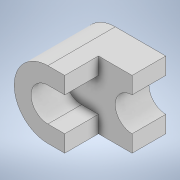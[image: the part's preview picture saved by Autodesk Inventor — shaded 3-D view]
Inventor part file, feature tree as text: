
AUTODESK INVENTOR PART (.ipt)
format: ipt  version: 2020 (Build 240168000, 168)  size: 124,416 bytes
history: native  units: mm
features: extrude x2, sketch x2, other x1
ambient origin geometry x8: Origin, YZ Plane, XZ Plane, XY Plane, X Axis, Y Axis, Z Axis, Center Point
bodies: Body1 (feature_tree)
feature tree (5):
  other  "實體1"
  extrude  "擠出1"  Depth=40.0mm
  extrude  "擠出2"  Depth=20.0mm
  sketch  "草圖1"
  sketch  "草圖2"
